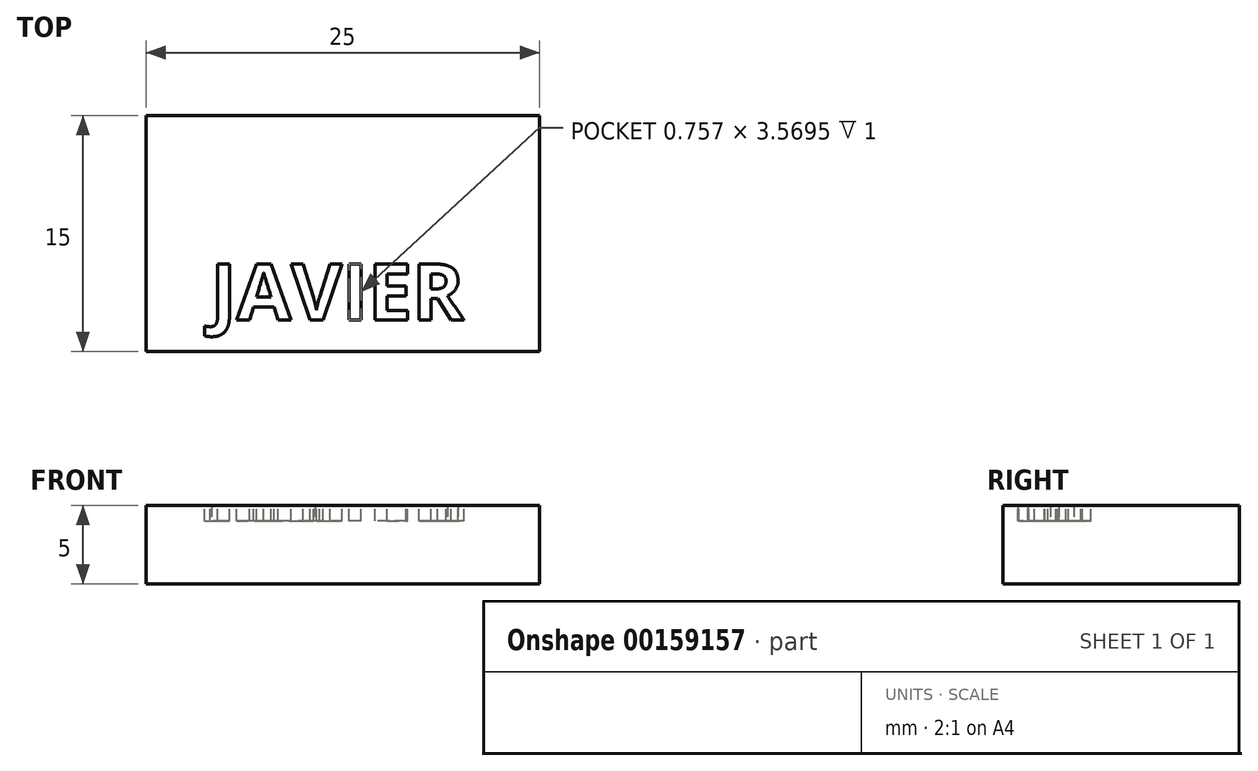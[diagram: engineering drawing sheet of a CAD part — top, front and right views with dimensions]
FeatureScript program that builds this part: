
annotation { "Feature Type Name" : "Feature", "Feature Type Description" : "" }
export const myFeature = defineFeature(function(context is Context, id is Id, definition is map)
    precondition{}
    {
        {
            var Q0;
            Q0=qCreatedBy(makeId("Top.planeOp"),FACE);
            var sketch = newSketch(context, id + "F0", { "sketchPlane" : qUnion([Q0])});
            skLineSegment(sketch, "E0.bottom", {"start": v(12.5, 7.5) * mm, "end": v(-12.5, 7.5) * mm});
            skLineSegment(sketch, "E0.top", {"start": v(12.5, -7.5) * mm, "end": v(-12.5, -7.5) * mm});
            skLineSegment(sketch, "E0.left", {"start": v(12.5, 7.5) * mm, "end": v(12.5, -7.5) * mm});
            skLineSegment(sketch, "E0.right", {"start": v(-12.5, 7.5) * mm, "end": v(-12.5, -7.5) * mm});
            skPoint(sketch, "E0.middle", {"position": v(0, 0) * mm});
            skSolve(sketch);
        }
        {
            var Q0;
            Q0 = qSketchRegion(id + "F0", true);
            extrude(context, id + "F1", {"entities" : qUnion([Q0]), "depth" : 5 * mm});
        }
        {
            var Q0;
            Q0=makeQuery(id+"F1.opExtrude","CAP_FACE",FACE,{"disambiguationData":[OSD([sQuery(id+"F0.wireOp",EDGE,"E0.bottom"),sQuery(id+"F0.wireOp",EDGE,"E0.top"),sQuery(id+"F0.wireOp",EDGE,"E0.left"),sQuery(id+"F0.wireOp",EDGE,"E0.right")])],"isStart":false});
            var sketch = newSketch(context, id + "F2", { "sketchPlane" : qUnion([Q0])});
            skText(sketch, "E1", { "text": "JAVIER", "fontName": "OpenSans-Bold.ttf"});
            const initialGuessF2  = {"E1": [-0.0084, -0.0055, 1, 0, 0.0036]};
            skSetInitialGuess(sketch, initialGuessF2);
            skSolve(sketch);
        }
        {
            var Q0;
            Q0 = qSketchRegion(id + "F2", true);
            extrude(context, id + "F3", {"entities" : qUnion([Q0]), "operationType" : NewBodyOperationType.REMOVE, "oppositeDirection" : true, "depth" : 1 * mm});
        }
    });
